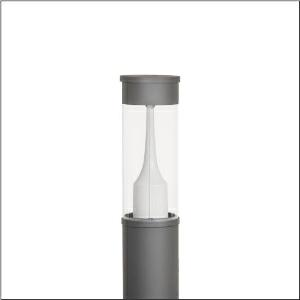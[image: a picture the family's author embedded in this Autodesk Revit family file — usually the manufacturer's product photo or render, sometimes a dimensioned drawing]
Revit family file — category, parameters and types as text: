
# Revit family: city-light_120_iq___pl1_2s_5xa5285cf14h_ce3b
name_source: partatom
category: Lighting Fixtures
units: mm (PartAtom-declared; Revit-internal decimal feet)

## family parameters
Cut with Voids When Loaded = No
Host = Face
Light Source = No
Part Type = Normal
Room Calculation Point = No
Round Connector Dimension = Use Diameter
Shared = No

## types (1)
- --- (1 x LED, 2970 lm, 23.9 W, 2200K)
    Apparent Load = 24 VA
    CIE Flux Codes = 23 62 94 96 100
    Color Rendering = 70
    Color Temperature = 2200K
    Default Elevation = 1800 mm
    Description = City-Light 120 iQ, bollard luminaire, Module 540 iQ-SR, primary light control with 3 zone facetted reflector, of plastic, silver coated, highly specular, structured, primary optical cover: cover, of PMMA, transparent, partly coated, light distribution: PL1.2s, primary light characteristic: symmetric, LED, High Power LED, rated luminous flux: 2.970lm, luminous efficacy: 124lm/W, light colour: 722, colour temperature: 2200K, control gear: ECG iQ, control: presetting dimming logarithmic, Street-Remote, Auto-Match, Temp-Guard, Lumen-Switch, Night-Set, Smart-Wire, Light-Fading, Desk-Remote (wireless, voltage-free reading and setting of iQ features in the workshop via application-optimized NFC function/RFID function), optimised constant luminous flux control (CLO 2.0), with terminal, 6-pole, max. 2.5mm², mains connection: 230..240V, AC, 50/60Hz, start of lifetime: 24W, end of service life: 26W, reduction: 12W, luminaire housing, cylindrical, of extruded aluminium section, coated, Siteco® metallic grey (DB 702S), length: 1.200mm, diameter: 200mm, Module 540 iQ-SR, traffic white (RAL 9016), equipment: standard, protection rating (complete): IP54, insulation class (complete): insulation class II (safety insulation), certification: CE, ENEC, VDE, packaging unit: 1 piece

Light Distribution: PL1.2s
    Height = 500 mm
    Lamp = 1 x LED
    Lamp Light Flux = 2970 lm
    Lamp Power = 23.9 W
    Lamp count = 1
    Length = 200 mm  [stored 0.656168 ft]
    Luminous efficacy = 124 lm/W
    Manufacturer = Siteco
    ModVariant = No
    Model = 5XA5285CF14H
    Mounting Place = Floor
    Mounting Type = Freestanding
    Number of Poles = 1
    OnlyDefault = Yes
    Power Factor = 1
    Product Name = City-Light 120 iQ | PL1.2s
    Product group = bollard luminaire
    ProductGroupID = 1304
    Protection Class = Protection class II
    Protection Degree = IP 54
    RLX_Detail_Level = 1
    RLX_Emergency_Light_Flux = 0 lm
    RLX_Emergency_Type = 0
    RLX_Emergency_Type_DB = No
    RlxData = <blob elided: 30445 chars, md5=3e09fc1b>
    Socket = socket
    Standby Power = 0 W
    System Light Flux = 2970 lm
    System Power = 24 W
    Type Comments = factory setting: luminous flux: 100 % | dim-lin: 254 | 499 mA
    Type Image = l_1006922.jpg
    URL = http://relux.com
    VarID = @adj_094797
    Voltage = 0 V
    Weight = 0.00 kg
    Width = 0 mm  [stored 0 ft]

note: [stored X ft] marks values corroborated as IEEE doubles in the binary element streams (Revit-internal decimal feet)

## geometry (parser evidence)
native form markers: Blend x4, Sweep x9
no freeform markers — native parametric forms only
